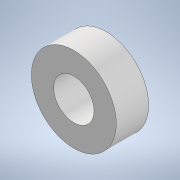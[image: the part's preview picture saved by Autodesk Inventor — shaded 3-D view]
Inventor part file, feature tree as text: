
AUTODESK INVENTOR PART (.ipt)
format: ipt  version: 2022 (Build 260153000, 153)  size: 99,840 bytes
history: native  units: in
note: dims shown in document units (in); Inventor stores cm internally (conversion verified against a paired STEP export)
features: extrude x1, sketch x1
ambient origin geometry x8: Origin, YZ Plane, XZ Plane, XY Plane, X Axis, Y Axis, Z Axis, Center Point
bodies: Solid1 (feature_tree)
feature tree (2):
  extrude  "Extrusion1"  Depth=0.3937in
  sketch  "Sketch1"  dims[d0=0.8268in d1=0.3937in d2=0.315in d3=0.0in]
